# Revit family: AC-C6T
name_source: partatom
category: Communication Devices
revit_build: Autodesk Revit 2014 (Build: 20130308_1515(x64)
units: mm (PartAtom-declared; Revit-internal decimal feet)

## types (1)
- AC-C6T
    100V Taps = 30, 15, 7.5, 3.8
    70V Taps = 30, 15, 7.5, 3.7, 1.9
    Coverage Horizontal = 110.00°
    Coverage Vertical = 110.00°
    Default Elevation = 0"
    Depth = 9.9498"
    Description = 6" Coaxial 2-way Loudspeaker Element
    Enclosure Depth = 7.9921"
    Enclosure Radius = 4.3898"
    Grille Depth = 0.3937"
    Grille Radius Base = 5.1181"
    Grille Radius Extent = 4.6063"
    Impedance = 8
    Manufacturer = QSC Audio Products, LLC
    Manufacturer URL = www.qscaudio.com
    Middle Depth = 1.564"
    Middle Radius = 4.9016"
    Model = AC-C6T
    Power Handling = 30
    Product Documentation Link = http://media.qscaudio.com
    Product Page URL = http://www.qscaudio.com
    Regulatory Compliance = RoHS, UL1480, UL2043
    SPL Max = 110
    Sensitivity = 89
    URL = http://www.qscaudio.com
    Weight Dimensional (kg) = 9.5
    Weight Dimensional (lb) = 21
    Weight Product (kg) = 3.5
    Weight Product (lb) = 7.6
    Width = 10.2362"

## geometry (parser evidence)
native form markers: Blend x11, Sweep x1
no freeform markers — native parametric forms only
